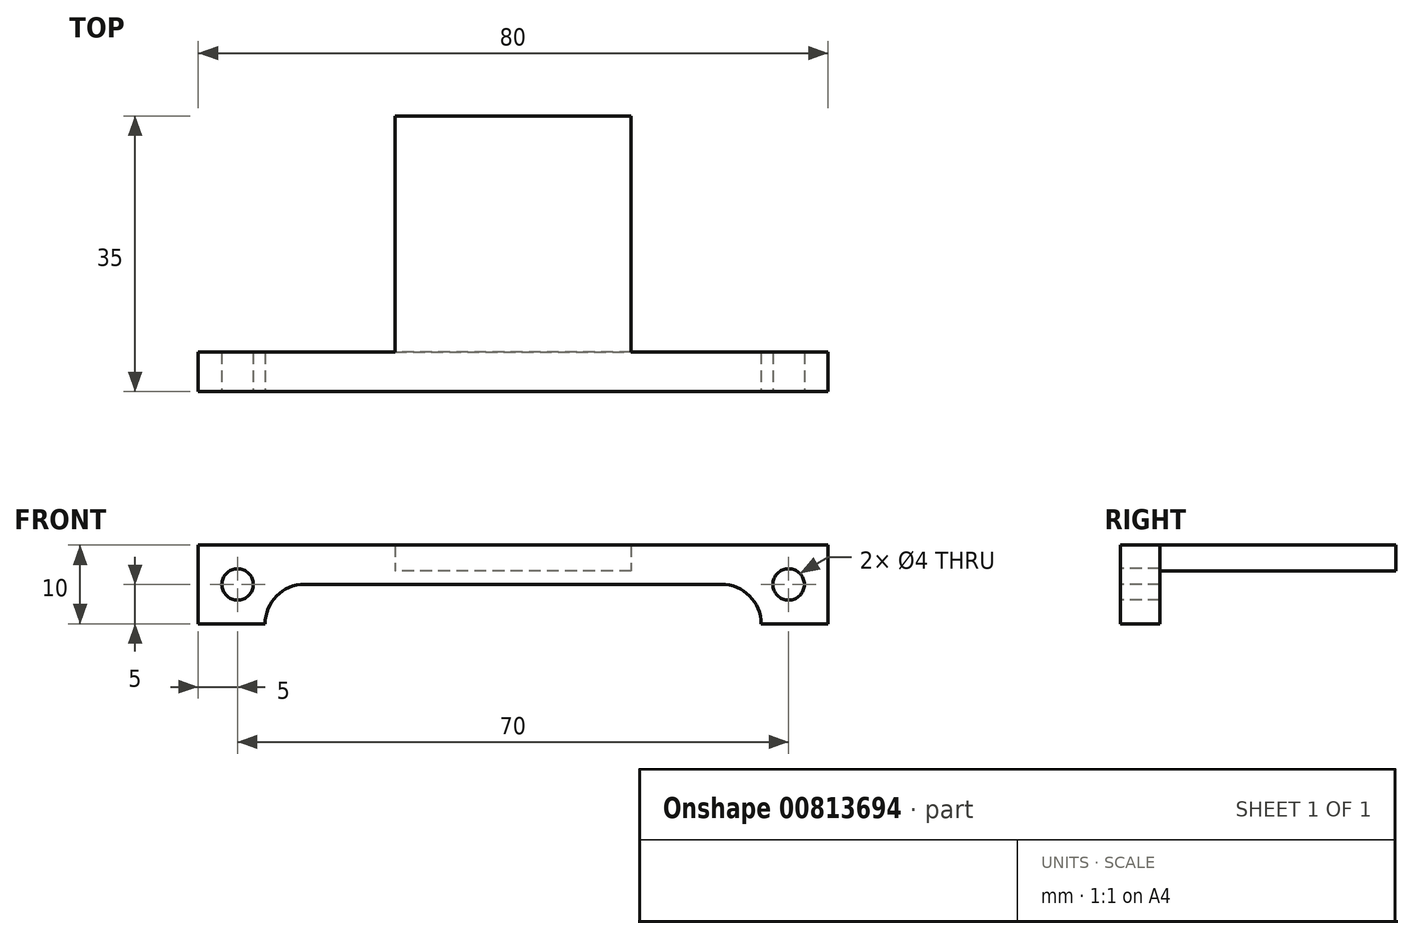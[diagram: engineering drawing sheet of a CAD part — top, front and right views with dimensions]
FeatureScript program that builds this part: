
annotation { "Feature Type Name" : "Feature", "Feature Type Description" : "" }
export const myFeature = defineFeature(function(context is Context, id is Id, definition is map)
    precondition{}
    {
        {
            var Q0;
            Q0=qCreatedBy(makeId("Top.planeOp"),FACE);
            var sketch = newSketch(context, id + "F0", { "sketchPlane" : qUnion([Q0])});
            skLineSegment(sketch, "E0.bottom", {"start": v(-40, 0) * mm, "end": v(40, 0) * mm});
            skLineSegment(sketch, "E0.top", {"start": v(-40, 5) * mm, "end": v(40, 5) * mm});
            skLineSegment(sketch, "E0.left", {"start": v(-40, 0) * mm, "end": v(-40, 5) * mm});
            skLineSegment(sketch, "E0.right", {"start": v(40, 0) * mm, "end": v(40, 5) * mm});
            skSolve(sketch);
        }
        {
            var Q0;
            Q0 = qSketchRegion(id + "F0", true);
            extrude(context, id + "F1", {"entities" : qUnion([Q0]), "depth" : 10 * mm, "offsetDistance" : 25 * mm});
        }
        {
            var Q0;
            Q0=makeQuery(id+"F1.opExtrude","SWEPT_FACE",FACE,{"disambiguationData":[OSD([sQuery(id+"F0.wireOp",EDGE,"E0.bottom")])]});
            var sketch = newSketch(context, id + "F2", { "sketchPlane" : qUnion([Q0])});
            skLineSegment(sketch, "E1", {"start": v(0, 0) * mm, "end": v(0, 5) * mm, "construction": true});
            skCircle(sketch, "E2", {"center": v(35, 5) * mm, "radius": 2 * mm});
            skPoint(sketch, "E2.centerSnap0", {"position": v(40, 5) * mm});
            skCircle(sketch, "E3", {"center": v(-35, 5) * mm, "radius": 2 * mm});
            skPoint(sketch, "E3.centerSnap0", {"position": v(-40, 5) * mm});
            skLineSegment(sketch, "E4", {"start": v(-35, 5) * mm, "end": v(35, 5) * mm, "construction": true});
            skLineSegment(sketch, "E5.bottom", {"start": v(-25, 5) * mm, "end": v(25, 5) * mm});
            skLineSegment(sketch, "E5.top", {"start": v(-25, 0) * mm, "end": v(25, 0) * mm});
            skLineSegment(sketch, "E6", {"start": v(31.5, 0) * mm, "end": v(31.5, 0) * mm});
            skLineSegment(sketch, "E7", {"start": v(26.5, 5) * mm, "end": v(-26.5, 5) * mm});
            skLineSegment(sketch, "E8", {"start": v(-31.5, 0) * mm, "end": v(-31.5, 0) * mm});
            skPoint(sketch, "E9.visualSharp", {"position": v(-31.5, 5) * mm});
            skArc(sketch, "E9.filletArc", {"start": v(-26.5, 5) * mm, "mid": v(-30.04, 3.54) * mm, "end": v(-31.5, 0) * mm});
            skPoint(sketch, "E10.visualSharp", {"position": v(31.5, 5) * mm});
            skArc(sketch, "E10.filletArc", {"start": v(31.5, 0) * mm, "mid": v(30.04, 3.54) * mm, "end": v(26.5, 5) * mm});
            skSolve(sketch);
        }
        {
            var Q0;
            Q0 = qSketchRegion(id + "F2", true);
            var Q1;
            {var subQ5=sQuery(id+"F2.wireOp",EDGE,"E5.top");Q1=makeQuery(id+"F2.imprint","IMPRINT",FACE,{"disambiguationData":[TD([[makeQuery(id+"F2.imprint","IMPRINT",EDGE,{"derivedFrom":subQ5}),1.0]])]});}
            extrude(context, id + "F3", {"entities" : qUnion([Q0, Q1]), "operationType" : NewBodyOperationType.REMOVE, "endBound" : BoundingType.THROUGH_ALL, "oppositeDirection" : true, "depth" : 25 * mm, "offsetDistance" : 25 * mm});
        }
        {
            var Q0;
            Q0=makeQuery(id+"F1.opExtrude","SWEPT_FACE",FACE,{"disambiguationData":[OSD([sQuery(id+"F0.wireOp",EDGE,"E0.top")])]});
            var sketch = newSketch(context, id + "F4", { "sketchPlane" : qUnion([Q0])});
            skLineSegment(sketch, "E11.bottom", {"start": v(-15, 10) * mm, "end": v(15, 10) * mm});
            skLineSegment(sketch, "E11.top", {"start": v(-15, 6.7) * mm, "end": v(15, 6.7) * mm});
            skLineSegment(sketch, "E11.left", {"start": v(-15, 10) * mm, "end": v(-15, 6.7) * mm});
            skLineSegment(sketch, "E11.right", {"start": v(15, 10) * mm, "end": v(15, 6.7) * mm});
            skSolve(sketch);
        }
        {
            var Q0;
            Q0 = qSketchRegion(id + "F4", true);
            extrude(context, id + "F5", {"entities" : qUnion([Q0]), "operationType" : NewBodyOperationType.ADD, "depth" : 30 * mm, "offsetDistance" : 25 * mm});
        }
    });
